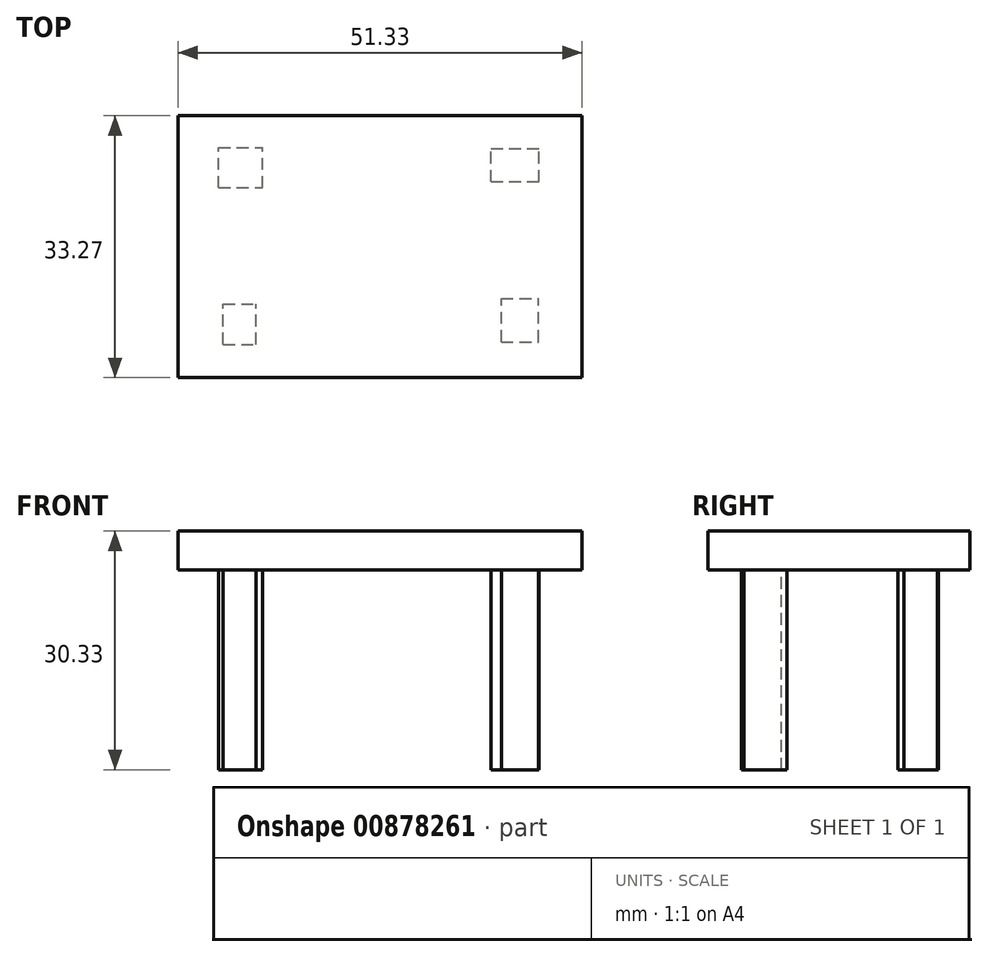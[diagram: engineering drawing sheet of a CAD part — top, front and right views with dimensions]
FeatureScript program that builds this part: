
annotation { "Feature Type Name" : "Feature", "Feature Type Description" : "" }
export const myFeature = defineFeature(function(context is Context, id is Id, definition is map)
    precondition{}
    {
        {
            var Q0;
            Q0=qCreatedBy(makeId("Front.planeOp"),FACE);
            var sketch = newSketch(context, id + "F0", { "sketchPlane" : qUnion([Q0])});
            skLineSegment(sketch, "E0.bottom", {"start": v(-70.87, 17.05) * mm, "end": v(-19.54, 17.05) * mm});
            skLineSegment(sketch, "E0.top", {"start": v(-70.87, 12.12) * mm, "end": v(-19.54, 12.12) * mm});
            skLineSegment(sketch, "E0.left", {"start": v(-70.87, 17.05) * mm, "end": v(-70.87, 12.12) * mm});
            skLineSegment(sketch, "E0.right", {"start": v(-19.54, 17.05) * mm, "end": v(-19.54, 12.12) * mm});
            skSolve(sketch);
        }
        {
            var Q0;
            Q0 = qSketchRegion(id + "F0", true);
            extrude(context, id + "F1", {"entities" : qUnion([Q0]), "depth" : 33.27 * mm, "offsetDistance" : 25.4 * mm});
        }
        {
            var Q0;
            Q0=makeQuery(id+"F1.opExtrude","SWEPT_FACE",FACE,{"disambiguationData":[OSD([sQuery(id+"F0.wireOp",EDGE,"E0.top")])]});
            var sketch = newSketch(context, id + "F2", { "sketchPlane" : qUnion([Q0])});
            skLineSegment(sketch, "E1.bottom", {"start": v(-65.14, 29.07) * mm, "end": v(-61, 29.07) * mm});
            skLineSegment(sketch, "E1.top", {"start": v(-65.14, 23.94) * mm, "end": v(-61, 23.94) * mm});
            skLineSegment(sketch, "E1.left", {"start": v(-65.14, 29.07) * mm, "end": v(-65.14, 23.94) * mm});
            skLineSegment(sketch, "E1.right", {"start": v(-61, 29.07) * mm, "end": v(-61, 23.94) * mm});
            skSolve(sketch);
        }
        {
            var Q0;
            Q0 = qSketchRegion(id + "F2", true);
            extrude(context, id + "F3", {"entities" : qUnion([Q0]), "operationType" : NewBodyOperationType.ADD, "depth" : 25.4 * mm, "offsetDistance" : 25.4 * mm});
        }
        {
            var Q0;
            Q0=makeQuery(id+"F1.opExtrude","SWEPT_FACE",FACE,{"disambiguationData":[OSD([sQuery(id+"F0.wireOp",EDGE,"E0.top")])]});
            var sketch = newSketch(context, id + "F4", { "sketchPlane" : qUnion([Q0])});
            skLineSegment(sketch, "E2.bottom", {"start": v(-29.8, 28.73) * mm, "end": v(-25.07, 28.73) * mm});
            skLineSegment(sketch, "E2.top", {"start": v(-29.8, 23.26) * mm, "end": v(-25.07, 23.26) * mm});
            skLineSegment(sketch, "E2.left", {"start": v(-29.8, 28.73) * mm, "end": v(-29.8, 23.26) * mm});
            skLineSegment(sketch, "E2.right", {"start": v(-25.07, 28.73) * mm, "end": v(-25.07, 23.26) * mm});
            skSolve(sketch);
        }
        {
            var Q0;
            Q0 = qSketchRegion(id + "F4", true);
            extrude(context, id + "F5", {"entities" : qUnion([Q0]), "operationType" : NewBodyOperationType.ADD, "depth" : 25.4 * mm, "offsetDistance" : 25.4 * mm});
        }
        {
            var Q0;
            Q0=makeQuery(id+"F1.opExtrude","SWEPT_FACE",FACE,{"disambiguationData":[OSD([sQuery(id+"F0.wireOp",EDGE,"E0.top")])]});
            var sketch = newSketch(context, id + "F6", { "sketchPlane" : qUnion([Q0])});
            skLineSegment(sketch, "E3.bottom", {"start": v(-65.73, 9.16) * mm, "end": v(-60.15, 9.16) * mm});
            skLineSegment(sketch, "E3.top", {"start": v(-65.73, 4.04) * mm, "end": v(-60.15, 4.04) * mm});
            skLineSegment(sketch, "E3.left", {"start": v(-65.73, 9.16) * mm, "end": v(-65.73, 4.04) * mm});
            skLineSegment(sketch, "E3.right", {"start": v(-60.15, 9.16) * mm, "end": v(-60.15, 4.04) * mm});
            skSolve(sketch);
        }
        {
            var Q0;
            Q0 = qSketchRegion(id + "F6", true);
            extrude(context, id + "F7", {"entities" : qUnion([Q0]), "operationType" : NewBodyOperationType.ADD, "depth" : 25.4 * mm, "offsetDistance" : 25.4 * mm});
        }
        {
            var Q0;
            Q0=makeQuery(id+"F1.opExtrude","SWEPT_FACE",FACE,{"disambiguationData":[OSD([sQuery(id+"F0.wireOp",EDGE,"E0.top")])]});
            var sketch = newSketch(context, id + "F8", { "sketchPlane" : qUnion([Q0])});
            skLineSegment(sketch, "E4.bottom", {"start": v(-31.13, 8.38) * mm, "end": v(-25.05, 8.38) * mm});
            skLineSegment(sketch, "E4.top", {"start": v(-31.13, 4.15) * mm, "end": v(-25.05, 4.15) * mm});
            skLineSegment(sketch, "E4.left", {"start": v(-31.13, 8.38) * mm, "end": v(-31.13, 4.15) * mm});
            skLineSegment(sketch, "E4.right", {"start": v(-25.05, 8.38) * mm, "end": v(-25.05, 4.15) * mm});
            skSolve(sketch);
        }
        {
            var Q0;
            Q0 = qSketchRegion(id + "F8", true);
            extrude(context, id + "F9", {"entities" : qUnion([Q0]), "operationType" : NewBodyOperationType.ADD, "depth" : 25.4 * mm, "offsetDistance" : 25.4 * mm});
        }
    });
